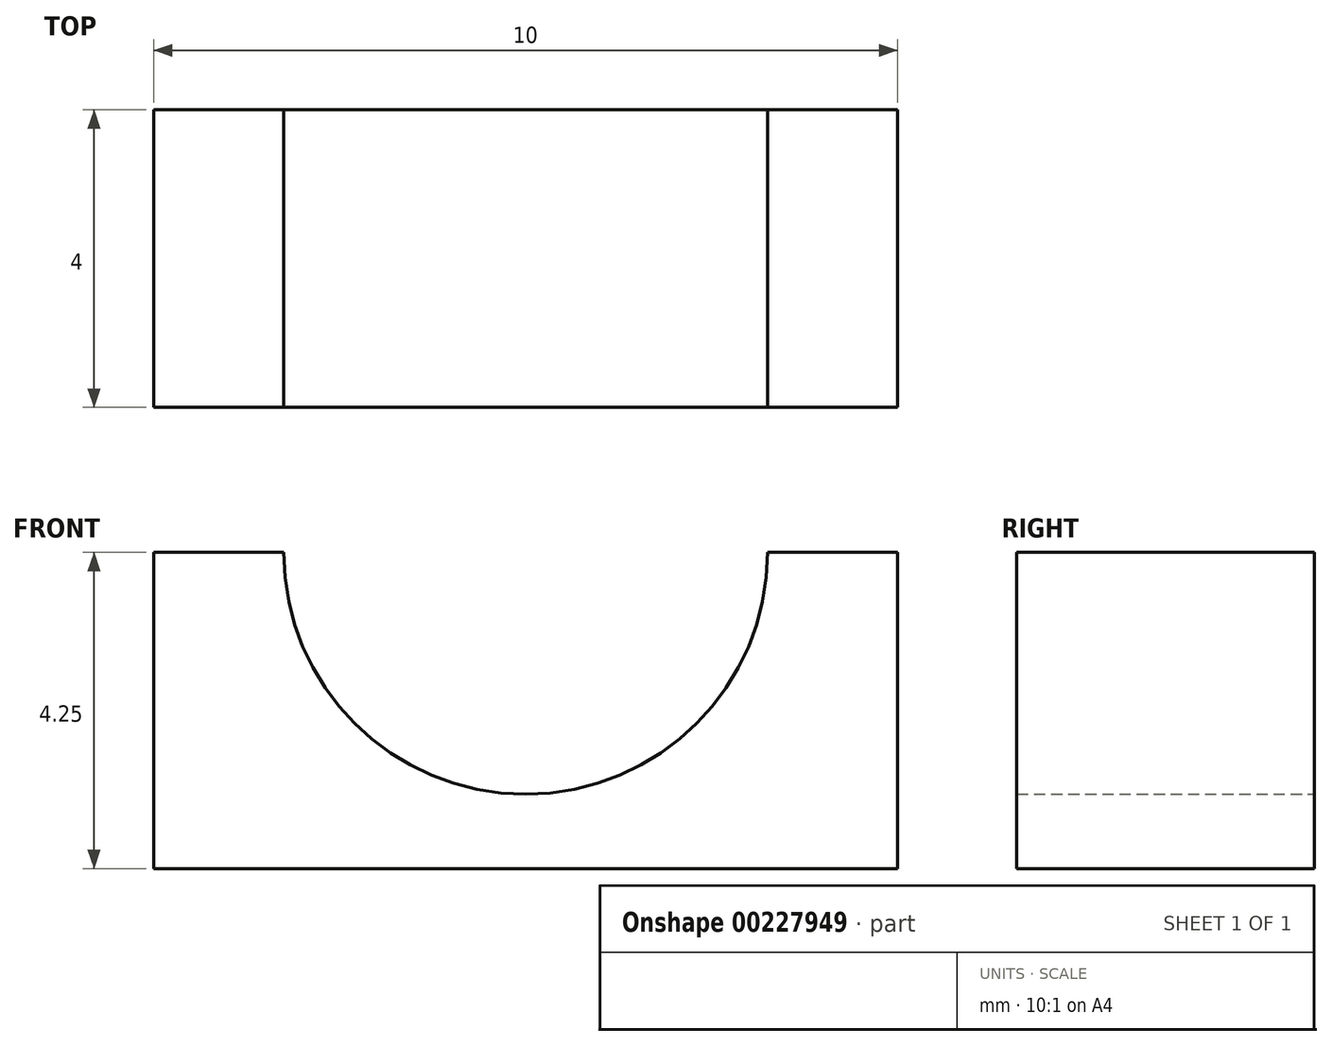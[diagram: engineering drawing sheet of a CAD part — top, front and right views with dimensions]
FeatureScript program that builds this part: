
annotation { "Feature Type Name" : "Feature", "Feature Type Description" : "" }
export const myFeature = defineFeature(function(context is Context, id is Id, definition is map)
    precondition{}
    {
        {
            var Q0;
            Q0=qCreatedBy(makeId("Front.planeOp"),FACE);
            var sketch = newSketch(context, id + "F0", { "sketchPlane" : qUnion([Q0])});
            skLineSegment(sketch, "E0", {"start": v(-5, 0) * mm, "end": v(5, 0) * mm});
            skLineSegment(sketch, "E1", {"start": v(0, 0) * mm, "end": v(0, 1) * mm, "construction": true});
            skLineSegment(sketch, "E2", {"start": v(0, 1) * mm, "end": v(0, 7.5) * mm, "construction": true});
            skArc(sketch, "E3", {"start": v(-3.25, 4.25) * mm, "mid": v(0, 1) * mm, "end": v(3.25, 4.25) * mm});
            skLineSegment(sketch, "E4", {"start": v(-5, 4.25) * mm, "end": v(-3.25, 4.25) * mm});
            skLineSegment(sketch, "E5", {"start": v(5, 4.25) * mm, "end": v(5, 0) * mm});
            skLineSegment(sketch, "E6", {"start": v(-5, 0) * mm, "end": v(-5, 4.25) * mm});
            skLineSegment(sketch, "E7.trimOffspring", {"start": v(3.25, 4.25) * mm, "end": v(5, 4.25) * mm});
            skSolve(sketch);
        }
        {
            var Q0;
            Q0 = qSketchRegion(id + "F0", true);
            extrude(context, id + "F1", {"entities" : qUnion([Q0]), "depth" : 4 * mm});
        }
    });
